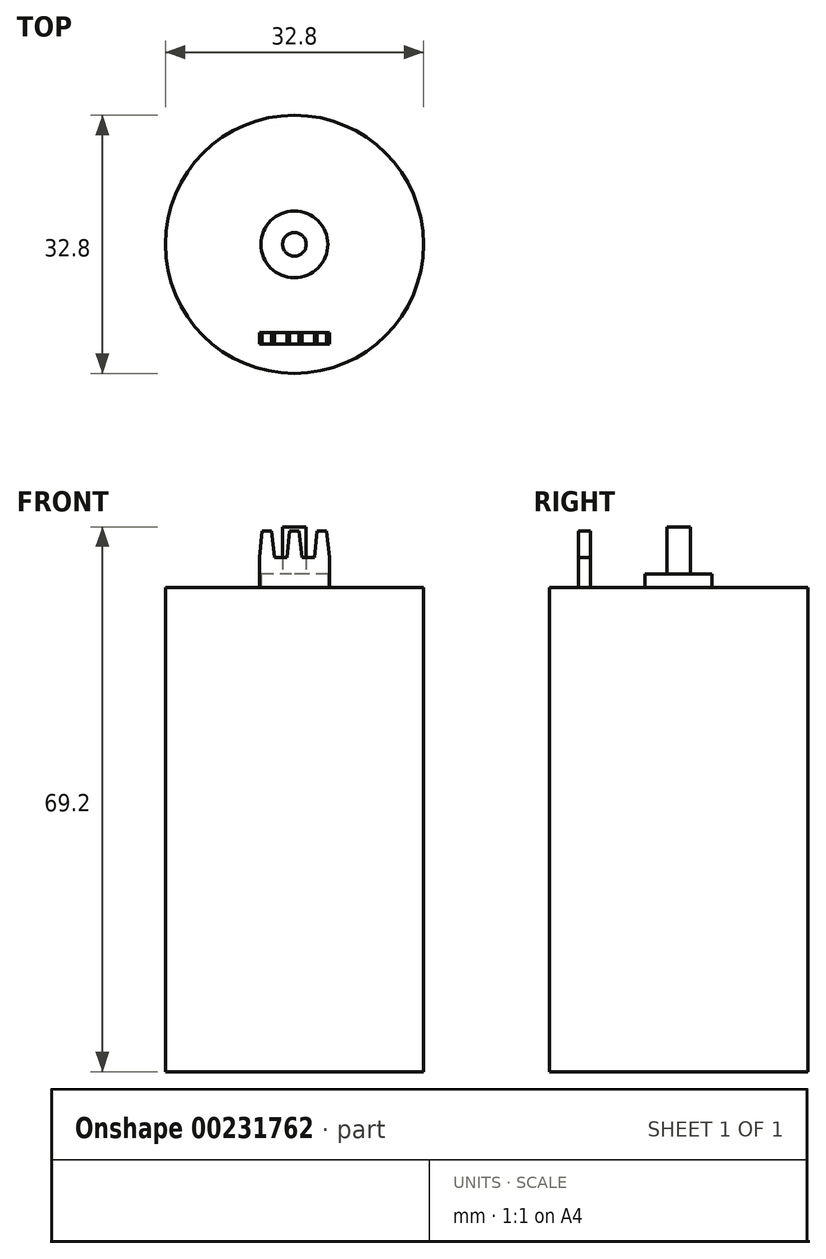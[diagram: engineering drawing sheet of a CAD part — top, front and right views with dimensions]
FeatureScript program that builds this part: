
annotation { "Feature Type Name" : "Feature", "Feature Type Description" : "" }
export const myFeature = defineFeature(function(context is Context, id is Id, definition is map)
    precondition{}
    {
        {
            var Q0;
            Q0=qCreatedBy(makeId("Top.planeOp"),FACE);
            var sketch = newSketch(context, id + "F0", { "sketchPlane" : qUnion([Q0])});
            skCircle(sketch, "E0", {"center": v(0, 0) * mm, "radius": 16.4 * mm});
            skSolve(sketch);
        }
        {
            var Q0;
            Q0=makeQuery(id+"F0.imprint","IMPRINT",FACE,{"disambiguationData":[TD([[makeQuery(id+"F0.imprint","IMPRINT",EDGE,{"derivedFrom":sQuery(id+"F0.wireOp",EDGE,"E0")}),1.0]])]});
            extrude(context, id + "F1", {"entities" : qUnion([Q0]), "depth" : 61.5 * mm});
        }
        {
            var Q0;
            Q0=makeQuery(id+"F1.opExtrude","CAP_FACE",FACE,{"disambiguationData":[OSD([sQuery(id+"F0.wireOp",EDGE,"E0")])],"isStart":false});
            var sketch = newSketch(context, id + "F2", { "sketchPlane" : qUnion([Q0])});
            skCircle(sketch, "E1", {"center": v(0, 0) * mm, "radius": 1.5 * mm});
            skSolve(sketch);
        }
        {
            var Q0;
            Q0=makeQuery(id+"F2.imprint","IMPRINT",FACE,{"disambiguationData":[TD([[makeQuery(id+"F2.imprint","IMPRINT",EDGE,{"derivedFrom":sQuery(id+"F2.wireOp",EDGE,"E1")}),1.0]])]});
            extrude(context, id + "F3", {"entities" : qUnion([Q0]), "operationType" : NewBodyOperationType.ADD, "depth" : 7.7 * mm});
        }
        {
            var Q0;
            Q0=makeQuery(id+"F1.opExtrude","CAP_FACE",FACE,{"disambiguationData":[OSD([sQuery(id+"F0.wireOp",EDGE,"E0")])],"isStart":false});
            var sketch = newSketch(context, id + "F4", { "sketchPlane" : qUnion([Q0])});
            skCircle(sketch, "E2", {"center": v(0, 0) * mm, "radius": 4.25 * mm});
            skSolve(sketch);
        }
        {
            var Q0;
            Q0=makeQuery(id+"F4.imprint","IMPRINT",FACE,{"disambiguationData":[TD([[makeQuery(id+"F4.imprint","IMPRINT",EDGE,{"derivedFrom":sQuery(id+"F4.wireOp",EDGE,"E2")}),1.0]])]});
            extrude(context, id + "F5", {"entities" : qUnion([Q0]), "operationType" : NewBodyOperationType.ADD, "depth" : 1.7 * mm});
        }
        {
            var Q0;
            Q0=makeQuery(id+"F1.opExtrude","CAP_FACE",FACE,{"disambiguationData":[OSD([sQuery(id+"F0.wireOp",EDGE,"E0")])],"isStart":false});
            var sketch = newSketch(context, id + "F6", { "sketchPlane" : qUnion([Q0])});
            skLineSegment(sketch, "E3.bottom", {"start": v(4.45, -12.69) * mm, "end": v(-4.45, -12.69) * mm});
            skLineSegment(sketch, "E3.top", {"start": v(4.45, -11.19) * mm, "end": v(-4.45, -11.19) * mm});
            skLineSegment(sketch, "E3.left", {"start": v(4.45, -12.69) * mm, "end": v(4.45, -11.19) * mm});
            skLineSegment(sketch, "E3.right", {"start": v(-4.45, -12.69) * mm, "end": v(-4.45, -11.19) * mm});
            skPoint(sketch, "E3.middle", {"position": v(0, -11.94) * mm});
            skSolve(sketch);
        }
        {
            var Q0;
            Q0=makeQuery(id+"F6.imprint","IMPRINT",FACE,{"disambiguationData":[TD([[makeQuery(id+"F6.imprint","IMPRINT",EDGE,{"derivedFrom":sQuery(id+"F6.wireOp",EDGE,"E3.bottom")}),-1.0]])]});
            extrude(context, id + "F7", {"entities" : qUnion([Q0]), "operationType" : NewBodyOperationType.ADD, "depth" : 7.2 * mm});
        }
        {
            var Q0;
            Q0=makeQuery(id+"F7.opExtrude","SWEPT_FACE",FACE,{"disambiguationData":[OSD([sQuery(id+"F6.wireOp",EDGE,"E3.bottom")])]});
            var sketch = newSketch(context, id + "F8", { "sketchPlane" : qUnion([Q0])});
            skLineSegment(sketch, "E4", {"start": v(0, 68.7) * mm, "end": v(0.6, 68.7) * mm});
            skLineSegment(sketch, "E5", {"start": v(0, 68.7) * mm, "end": v(0, 65.3) * mm, "construction": true});
            skLineSegment(sketch, "E6", {"start": v(0, 65.3) * mm, "end": v(0.95, 65.3) * mm, "construction": true});
            skLineSegment(sketch, "E7", {"start": v(0.6, 68.7) * mm, "end": v(0.95, 65.3) * mm});
            skLineSegment(sketch, "E8", {"start": v(0.95, 65.3) * mm, "end": v(2.55, 65.3) * mm});
            skLineSegment(sketch, "E9", {"start": v(2.55, 65.3) * mm, "end": v(2.9, 68.7) * mm});
            skLineSegment(sketch, "E10", {"start": v(2.9, 68.7) * mm, "end": v(4.1, 68.7) * mm});
            skLineSegment(sketch, "E11", {"start": v(4.1, 68.7) * mm, "end": v(4.45, 65.3) * mm});
            skLineSegment(sketch, "E12.MirrorCS", {"start": v(-4.1, 68.7) * mm, "end": v(-4.45, 65.3) * mm});
            skLineSegment(sketch, "E13.MirrorCS", {"start": v(-2.9, 68.7) * mm, "end": v(-4.1, 68.7) * mm});
            skLineSegment(sketch, "E14.MirrorCS", {"start": v(-2.55, 65.3) * mm, "end": v(-2.9, 68.7) * mm});
            skLineSegment(sketch, "E15.MirrorCS", {"start": v(-0.95, 65.3) * mm, "end": v(-2.55, 65.3) * mm});
            skLineSegment(sketch, "E16.MirrorCS", {"start": v(-0.6, 68.7) * mm, "end": v(-0.95, 65.3) * mm});
            skLineSegment(sketch, "E17.MirrorCS", {"start": v(0, 68.7) * mm, "end": v(-0.6, 68.7) * mm});
            skLineSegment(sketch, "E18", {"start": v(-4.45, 65.3) * mm, "end": v(-4.45, 68.7) * mm});
            skLineSegment(sketch, "E19", {"start": v(-4.45, 68.7) * mm, "end": v(4.45, 68.7) * mm});
            skLineSegment(sketch, "E20", {"start": v(4.45, 68.7) * mm, "end": v(4.45, 65.3) * mm});
            skSolve(sketch);
        }
        {
            var Q0;
            {var subQ0=sQuery(id+"F8.wireOp",EDGE,"E12.MirrorCS");Q0=makeQuery(id+"F8.imprint","IMPRINT",FACE,{"disambiguationData":[TD([[makeQuery(id+"F8.imprint","IMPRINT",EDGE,{"derivedFrom":subQ0}),-1.0]])]});}
            var Q1;
            {var subQ0=sQuery(id+"F8.wireOp",EDGE,"E14.MirrorCS");Q1=makeQuery(id+"F8.imprint","IMPRINT",FACE,{"disambiguationData":[TD([[makeQuery(id+"F8.imprint","IMPRINT",EDGE,{"derivedFrom":subQ0}),-1.0]])]});}
            var Q2;
            {var subQ0=sQuery(id+"F8.wireOp",EDGE,"E7");Q2=makeQuery(id+"F8.imprint","IMPRINT",FACE,{"disambiguationData":[TD([[makeQuery(id+"F8.imprint","IMPRINT",EDGE,{"derivedFrom":subQ0}),1.0]])]});}
            var Q3;
            {var subQ0=sQuery(id+"F8.wireOp",EDGE,"E11");Q3=makeQuery(id+"F8.imprint","IMPRINT",FACE,{"disambiguationData":[TD([[makeQuery(id+"F8.imprint","IMPRINT",EDGE,{"derivedFrom":subQ0}),1.0]])]});}
            var Q4;
            Q4=makeQuery(id+"F7.opExtrude","SWEPT_FACE",FACE,{"disambiguationData":[OSD([sQuery(id+"F6.wireOp",EDGE,"E3.top")])]});
            extrude(context, id + "F9", {"entities" : qUnion([Q0, Q1, Q2, Q3]), "operationType" : NewBodyOperationType.REMOVE, "endBound" : BoundingType.UP_TO_SURFACE, "oppositeDirection" : true, "endBoundEntityFace" : qUnion([Q4]), "depth" : 25 * mm});
        }
    });
